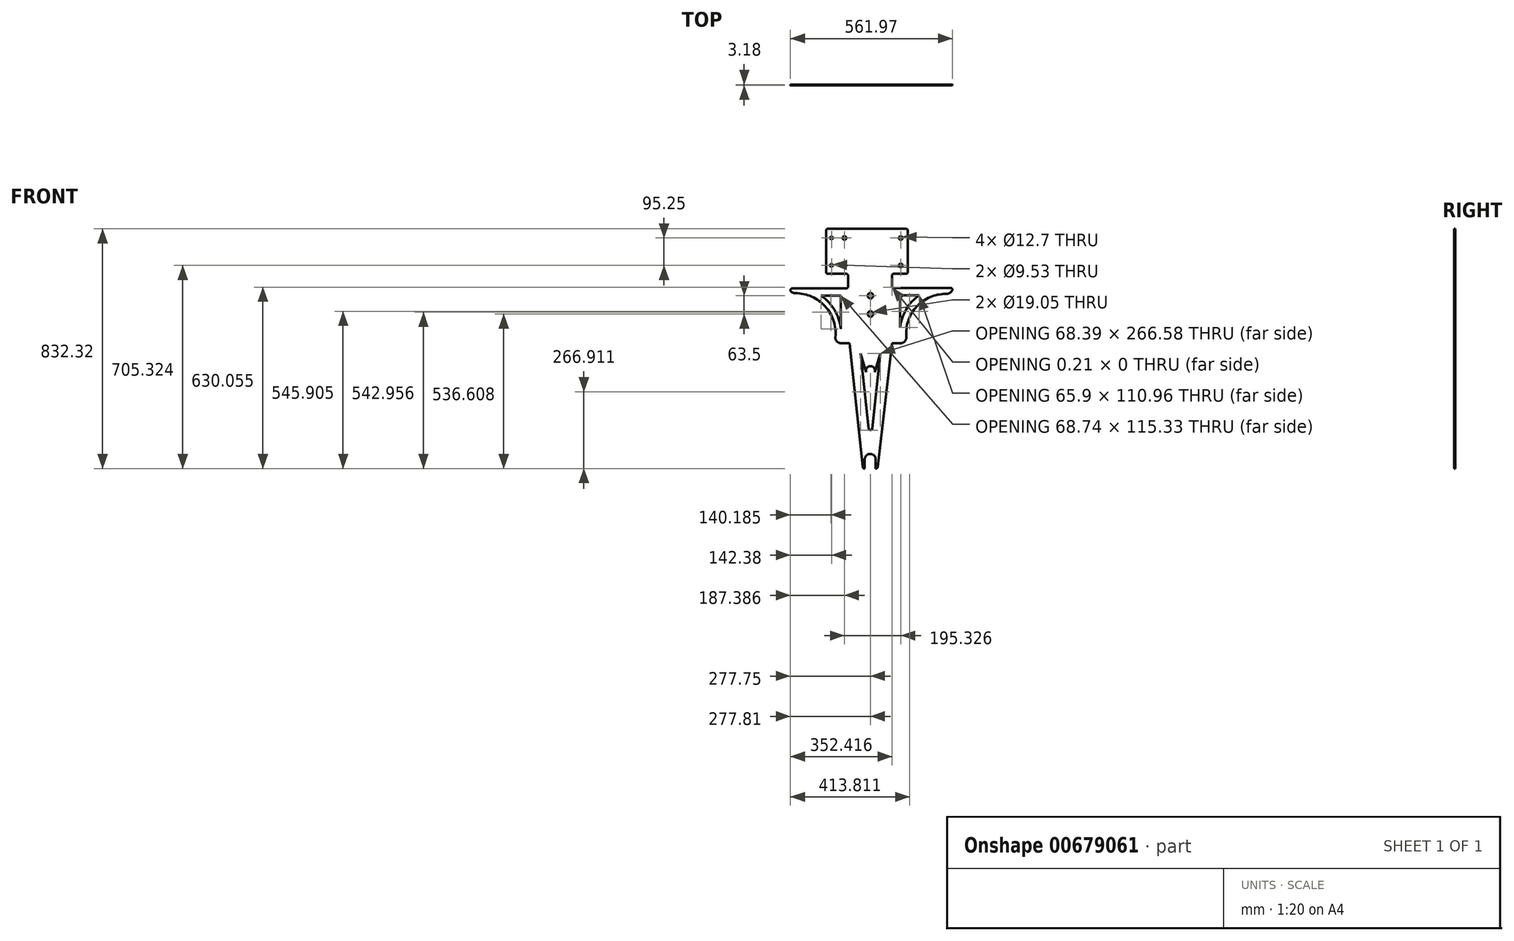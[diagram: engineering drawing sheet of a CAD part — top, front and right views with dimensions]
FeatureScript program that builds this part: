
annotation { "Feature Type Name" : "Feature", "Feature Type Description" : "" }
export const myFeature = defineFeature(function(context is Context, id is Id, definition is map)
    precondition{}
    {
        {
            var Q0;
            Q0=qCreatedBy(makeId("Front.planeOp"),FACE);
            var sketch = newSketch(context, id + "F0", { "sketchPlane" : qUnion([Q0])});
            skPoint(sketch, "E0.middle", {"position": v(0, 283.77) * mm});
            skLineSegment(sketch, "E1.bottom", {"start": v(277.79, 181.64) * mm, "end": v(123.63, 181.05) * mm});
            skPoint(sketch, "E1.middle", {"position": v(0, 90.78) * mm});
            skLineSegment(sketch, "E2.top", {"start": v(18.74, -445.83) * mm, "end": v(18.05, -445.83) * mm});
            skPoint(sketch, "E2.middle", {"position": v(0, -205.8) * mm});
            skPoint(sketch, "E3", {"position": v(-103.2, 29.26) * mm});
            skPoint(sketch, "E4", {"position": v(105.2, 29.26) * mm});
            skPoint(sketch, "E5", {"position": v(-298.6, 157.88) * mm});
            skPoint(sketch, "E6", {"position": v(285.82, 157.88) * mm});
            skPoint(sketch, "E7", {"position": v(-285.82, -0.1) * mm});
            skPoint(sketch, "E8", {"position": v(-260.42, 23.94) * mm});
            skPoint(sketch, "E9", {"position": v(259.88, 24.5) * mm});
            skArc(sketch, "E10", {"start": v(-121.82, 10.25) * mm, "mid": v(-157.17, 117.4) * mm, "end": v(-260.29, 163.22) * mm});
            skArc(sketch, "E11", {"start": v(261.59, 160.37) * mm, "mid": v(160.2, 116.86) * mm, "end": v(124.52, 12.46) * mm});
            skLineSegment(sketch, "E12.trimOffspring", {"start": v(103.11, -10.86) * mm, "end": v(-103.31, -10.24) * mm});
            skPoint(sketch, "E13.orphan", {"position": v(285.28, 2.06) * mm});
            skArc(sketch, "E14.filletArc", {"start": v(261.59, 160.37) * mm, "mid": v(273.8, 163.33) * mm, "end": v(283.11, 171.8) * mm});
            skArc(sketch, "E15.filletArc", {"start": v(-275.2, 168.07) * mm, "mid": v(-268.12, 164.46) * mm, "end": v(-260.29, 163.22) * mm});
            skPoint(sketch, "E16.visualSharp", {"position": v(-125.39, -10.17) * mm});
            skArc(sketch, "E16.filletArc", {"start": v(-121.82, 10.25) * mm, "mid": v(-117.1, -4.09) * mm, "end": v(-103.31, -10.24) * mm});
            skPoint(sketch, "E17.visualSharp", {"position": v(128.69, -10.94) * mm});
            skArc(sketch, "E17.filletArc", {"start": v(103.11, -10.86) * mm, "mid": v(118.96, -3.92) * mm, "end": v(124.52, 12.46) * mm});
            skPoint(sketch, "E18", {"position": v(-1, -445.83) * mm});
            skPoint(sketch, "E19", {"position": v(-26.4, -445.83) * mm});
            skPoint(sketch, "E20", {"position": v(24.4, -445.83) * mm});
            skLineSegment(sketch, "E21", {"start": v(-27.01, -440.16) * mm, "end": v(-73.02, -10.33) * mm});
            skLineSegment(sketch, "E22", {"start": v(25.05, -440.21) * mm, "end": v(74.6, -10.78) * mm});
            skPoint(sketch, "E23.orphan", {"position": v(-79.8, -445.83) * mm});
            skPoint(sketch, "E2.left.end.orphan", {"position": v(77.8, -445.83) * mm});
            skPoint(sketch, "E24", {"position": v(-1, -414.08) * mm});
            skArc(sketch, "E25", {"start": v(18.05, -414.08) * mm, "mid": v(-1, -395.03) * mm, "end": v(-20.05, -414.08) * mm});
            skPoint(sketch, "E26", {"position": v(-20.05, -445.83) * mm});
            skPoint(sketch, "E27", {"position": v(18.05, -445.83) * mm});
            skLineSegment(sketch, "E28", {"start": v(-20.05, -445.83) * mm, "end": v(-20.05, -414.08) * mm});
            skLineSegment(sketch, "E29.trimOffspring", {"start": v(-20.05, -445.83) * mm, "end": v(-20.7, -445.83) * mm});
            skArc(sketch, "E30.filletArc", {"start": v(-27.01, -440.16) * mm, "mid": v(-24.94, -444.2) * mm, "end": v(-20.7, -445.83) * mm});
            skArc(sketch, "E31.filletArc", {"start": v(18.74, -445.83) * mm, "mid": v(22.96, -444.22) * mm, "end": v(25.05, -440.21) * mm});
            skPoint(sketch, "E32", {"position": v(-234.86, 179.7) * mm});
            skArc(sketch, "E33", {"start": v(-103.26, 39.46) * mm, "mid": v(-124.76, 104.8) * mm, "end": v(-172, 154.8) * mm});
            skPoint(sketch, "E34", {"position": v(97.68, 155.55) * mm});
            skPoint(sketch, "E35", {"position": v(-103.26, 154.8) * mm});
            skLineSegment(sketch, "E36", {"start": v(103.18, 155.55) * mm, "end": v(168.95, 155.55) * mm});
            skLineSegment(sketch, "E37", {"start": v(-103.26, 154.8) * mm, "end": v(-172, 154.8) * mm});
            skPoint(sketch, "E38.orphan", {"position": v(97.68, -10.85) * mm});
            skArc(sketch, "E39.trimOffspring", {"start": v(168.95, 155.55) * mm, "mid": v(123.9, 107.26) * mm, "end": v(103.05, 44.6) * mm});
            skLineSegment(sketch, "E40", {"start": v(-103.26, 39.46) * mm, "end": v(-103.26, 154.8) * mm});
            skPoint(sketch, "E41", {"position": v(-0.1, -105.95) * mm});
            skPoint(sketch, "E41.positionSnap0", {"position": v(-0.1, -10.55) * mm});
            skPoint(sketch, "E42.orphan", {"position": v(-77.8, 34.23) * mm});
            skPoint(sketch, "E43.orphan", {"position": v(79.8, 34.23) * mm});
            skLineSegment(sketch, "E44", {"start": v(103.18, 45.74) * mm, "end": v(103.18, 155.55) * mm});
            skPoint(sketch, "E0.bottom.end.orphan", {"position": v(-123.62, 386.49) * mm});
            skLineSegment(sketch, "E45.right", {"start": v(129.75, 237.02) * mm, "end": v(129.75, 332.52) * mm});
            skLineSegment(sketch, "E46.trimOffspring", {"start": v(-234.86, 179.7) * mm, "end": v(-271.48, 179.55) * mm});
            skPoint(sketch, "E47.orphan", {"position": v(-285.28, 179.5) * mm});
            skPoint(sketch, "E48.orphan", {"position": v(285.82, 181.67) * mm});
            skPoint(sketch, "E49", {"position": v(-90.42, 307.12) * mm});
            skPoint(sketch, "E50", {"position": v(-90.42, 211.87) * mm});
            skPoint(sketch, "E51", {"position": v(96.86, 307.12) * mm});
            skPoint(sketch, "E52", {"position": v(96.86, 211.87) * mm});
            skLineSegment(sketch, "E53.trimOffspring", {"start": v(-116.38, 236.83) * mm, "end": v(-116.38, 332.52) * mm});
            skPoint(sketch, "E45.left.start.orphan", {"position": v(-115.82, 135.67) * mm});
            skPoint(sketch, "E54.orphan", {"position": v(-122.59, 180.12) * mm});
            skLineSegment(sketch, "E55", {"start": v(-234.86, 179.7) * mm, "end": v(-116.38, 179.68) * mm});
            skPoint(sketch, "E0.left.start.orphan", {"position": v(122.59, 387.42) * mm});
            skPoint(sketch, "E56", {"position": v(-0.1, -35.95) * mm});
            skPoint(sketch, "E57", {"position": v(0, -99.45) * mm});
            skPoint(sketch, "E58", {"position": v(-77.8, 179.68) * mm});
            skPoint(sketch, "E59", {"position": v(74.6, 181.05) * mm});
            skPoint(sketch, "E60", {"position": v(-77.8, 181.27) * mm});
            skPoint(sketch, "E61", {"position": v(74.6, 182.64) * mm});
            skArc(sketch, "E62", {"start": v(74.71, 184.22) * mm, "mid": v(74.6, 184.23) * mm, "end": v(74.5, 184.22) * mm});
            skLineSegment(sketch, "E63", {"start": v(74.5, 184.22) * mm, "end": v(74.71, 184.22) * mm});
            skLineSegment(sketch, "E64", {"start": v(80.96, 181.05) * mm, "end": v(123.6, 181.05) * mm});
            skPoint(sketch, "E65.orphan", {"position": v(129.75, 181.2) * mm});
            skLineSegment(sketch, "E66", {"start": v(103.18, 155.55) * mm, "end": v(103.05, 44.6) * mm});
            skPoint(sketch, "E67.end.orphan", {"position": v(-31.85, -87.3) * mm});
            skPoint(sketch, "E68.end.orphan", {"position": v(31.65, -87.3) * mm});
            skLineSegment(sketch, "E69", {"start": v(-24.38, -137.86) * mm, "end": v(-6.33, -306.54) * mm});
            skLineSegment(sketch, "E70", {"start": v(6.3, -306.53) * mm, "end": v(24.04, -140.26) * mm});
            skPoint(sketch, "E71.end.orphan", {"position": v(0, -301) * mm});
            skLineSegment(sketch, "E72", {"start": v(18.05, -414.08) * mm, "end": v(18.05, -445.83) * mm});
            skPoint(sketch, "E73", {"position": v(0, 179.68) * mm});
            skPoint(sketch, "E74", {"position": v(0, 154.28) * mm});
            skCircle(sketch, "E75", {"center": v(0, 154.28) * mm, "radius": 9.53 * mm});
            skCircle(sketch, "E76", {"center": v(0, 90.78) * mm, "radius": 9.53 * mm});
            skLineSegment(sketch, "E77", {"start": v(-24.38, -137.86) * mm, "end": v(-33.5, -52.65) * mm});
            skLineSegment(sketch, "E78", {"start": v(24.04, -140.26) * mm, "end": v(33.39, -52.65) * mm});
            skPoint(sketch, "E79.orphan", {"position": v(35.17, -35.95) * mm});
            skPoint(sketch, "E80.visualSharp", {"position": v(34.13, -45.63) * mm});
            skPoint(sketch, "E81.visualSharp", {"position": v(-34.26, -45.63) * mm});
            skPoint(sketch, "E82.visualSharp", {"position": v(0, -365.62) * mm});
            skArc(sketch, "E82.filletArc", {"start": v(-6.33, -306.54) * mm, "mid": v(0, -312.2) * mm, "end": v(6.3, -306.53) * mm});
            skPoint(sketch, "E83.visualSharp", {"position": v(-116.38, 338.87) * mm});
            skLineSegment(sketch, "E83.filletArc", {"start": v(-116.38, 332.52) * mm, "end": v(-116.38, 332.52) * mm});
            skPoint(sketch, "E84.visualSharp", {"position": v(129.75, 338.86) * mm});
            skPoint(sketch, "E85.visualSharp", {"position": v(123.62, 181.05) * mm});
            skArc(sketch, "E85.filletArc", {"start": v(123.6, 181.05) * mm, "mid": v(123.62, 181.05) * mm, "end": v(123.63, 181.05) * mm});
            skPoint(sketch, "E86.visualSharp", {"position": v(129.75, 184.22) * mm});
            skPoint(sketch, "E87.visualSharp", {"position": v(-116.38, 182.86) * mm});
            skPoint(sketch, "E88.visualSharp", {"position": v(-283.97, 179.5) * mm});
            skArc(sketch, "E88.filletArc", {"start": v(-271.48, 179.55) * mm, "mid": v(-277.5, 175.15) * mm, "end": v(-275.2, 168.07) * mm});
            skPoint(sketch, "E89.visualSharp", {"position": v(286.97, 181.67) * mm});
            skArc(sketch, "E89.filletArc", {"start": v(283.11, 171.8) * mm, "mid": v(283.4, 178.3) * mm, "end": v(277.79, 181.64) * mm});
            skPoint(sketch, "E90", {"position": v(104.9, 307.12) * mm});
            skPoint(sketch, "E91", {"position": v(104.9, 211.87) * mm});
            skLineSegment(sketch, "E92", {"start": v(-110.03, 386.49) * mm, "end": v(123.4, 386.49) * mm});
            skLineSegment(sketch, "E93", {"start": v(-116.38, 380.14) * mm, "end": v(-116.38, 332.52) * mm});
            skLineSegment(sketch, "E94", {"start": v(129.75, 380.14) * mm, "end": v(129.75, 332.52) * mm});
            skLineSegment(sketch, "E95", {"start": v(-110.03, 230.48) * mm, "end": v(-84.14, 230.48) * mm});
            skLineSegment(sketch, "E96", {"start": v(-77.8, 186.03) * mm, "end": v(-77.8, 224.13) * mm});
            skLineSegment(sketch, "E97", {"start": v(74.6, 187.4) * mm, "end": v(74.6, 224.24) * mm});
            skPoint(sketch, "E97.endSnap0", {"position": v(6.68, 230.58) * mm});
            skPoint(sketch, "E98.start.orphan", {"position": v(-77.8, 182.85) * mm});
            skLineSegment(sketch, "E99", {"start": v(123.4, 230.67) * mm, "end": v(80.94, 230.6) * mm});
            skCircle(sketch, "E100", {"center": v(-90.42, 354.74) * mm, "radius": 6.35 * mm});
            skCircle(sketch, "E101", {"center": v(104.9, 354.74) * mm, "radius": 6.35 * mm});
            skCircle(sketch, "E102", {"center": v(-90.42, 259.5) * mm, "radius": 6.35 * mm});
            skCircle(sketch, "E103", {"center": v(104.9, 259.5) * mm, "radius": 6.35 * mm});
            skPoint(sketch, "E104.visualSharp", {"position": v(74.6, 230.58) * mm});
            skArc(sketch, "E104.filletArc", {"start": v(80.94, 230.6) * mm, "mid": v(76.46, 228.73) * mm, "end": v(74.6, 224.24) * mm});
            skArc(sketch, "E105.filletArc", {"start": v(74.6, 187.4) * mm, "mid": v(76.47, 182.91) * mm, "end": v(80.96, 181.05) * mm});
            skPoint(sketch, "E106.visualSharp", {"position": v(129.75, 230.68) * mm});
            skArc(sketch, "E106.filletArc", {"start": v(123.4, 230.67) * mm, "mid": v(127.9, 232.53) * mm, "end": v(129.75, 237.02) * mm});
            skPoint(sketch, "E107.visualSharp", {"position": v(129.75, 386.49) * mm});
            skArc(sketch, "E107.filletArc", {"start": v(129.75, 380.14) * mm, "mid": v(127.89, 384.63) * mm, "end": v(123.4, 386.49) * mm});
            skPoint(sketch, "E108.visualSharp", {"position": v(-116.38, 386.49) * mm});
            skPoint(sketch, "E109.visualSharp", {"position": v(-116.38, 230.48) * mm});
            skPoint(sketch, "E110.visualSharp", {"position": v(-77.8, 230.48) * mm});
            skArc(sketch, "E110.filletArc", {"start": v(-77.8, 224.13) * mm, "mid": v(-79.65, 228.62) * mm, "end": v(-84.14, 230.48) * mm});
            skArc(sketch, "E111.filletArc", {"start": v(-84.14, 179.68) * mm, "mid": v(-79.65, 181.54) * mm, "end": v(-77.8, 186.03) * mm});
            skArc(sketch, "E112", {"start": v(15.13, -110.42) * mm, "mid": v(-0.1, -90.08) * mm, "end": v(-15.34, -110.4) * mm});
            skLineSegment(sketch, "E113", {"start": v(34.13, -45.63) * mm, "end": v(15.13, -110.42) * mm});
            skLineSegment(sketch, "E114", {"start": v(-34.26, -45.63) * mm, "end": v(-15.34, -110.4) * mm});
            skLineSegment(sketch, "E115", {"start": v(-34.26, -45.63) * mm, "end": v(-33.5, -52.65) * mm});
            skLineSegment(sketch, "E116", {"start": v(34.13, -45.63) * mm, "end": v(33.39, -52.65) * mm});
            skLineSegment(sketch, "E117", {"start": v(-84.14, 179.68) * mm, "end": v(-116.38, 179.68) * mm});
            skLineSegment(sketch, "E118", {"start": v(-154.48, 380.14) * mm, "end": v(-154.48, 236.83) * mm});
            skLineSegment(sketch, "E119", {"start": v(-148.13, 386.49) * mm, "end": v(-110.03, 386.49) * mm});
            skLineSegment(sketch, "E120", {"start": v(-148.13, 230.48) * mm, "end": v(-110.03, 230.48) * mm});
            skPoint(sketch, "E121.visualSharp", {"position": v(-154.48, 230.48) * mm});
            skArc(sketch, "E121.filletArc", {"start": v(-154.48, 236.83) * mm, "mid": v(-152.62, 232.34) * mm, "end": v(-148.13, 230.48) * mm});
            skPoint(sketch, "E122.visualSharp", {"position": v(-154.48, 386.49) * mm});
            skArc(sketch, "E122.filletArc", {"start": v(-148.13, 386.49) * mm, "mid": v(-152.62, 384.63) * mm, "end": v(-154.48, 380.14) * mm});
            skCircle(sketch, "E123", {"center": v(-135.43, 354.74) * mm, "radius": 4.76 * mm});
            skCircle(sketch, "E124", {"center": v(-135.43, 259.5) * mm, "radius": 4.76 * mm});
            skSolve(sketch);
        }
        {
            var Q0;
            Q0=makeQuery(id+"F0.imprint","IMPRINT",FACE,{"disambiguationData":[TD([[makeQuery(id+"F0.imprint","IMPRINT",EDGE,{"derivedFrom":sQuery(id+"F0.wireOp",EDGE,"E2.top")}),-1.0]])]});
            var Q1;
            Q1=makeQuery(id+"F0.imprint","IMPRINT",FACE,{"disambiguationData":[TD([[makeQuery(id+"F0.imprint","IMPRINT",EDGE,{"derivedFrom":sQuery(id+"F0.wireOp",EDGE,"E1.bottom")}),1.0]])]});
            extrude(context, id + "F1", {"entities" : qUnion([Q0, Q1]), "depth" : 3.17 * mm, "offsetDistance" : 25.4 * mm});
        }
    });
